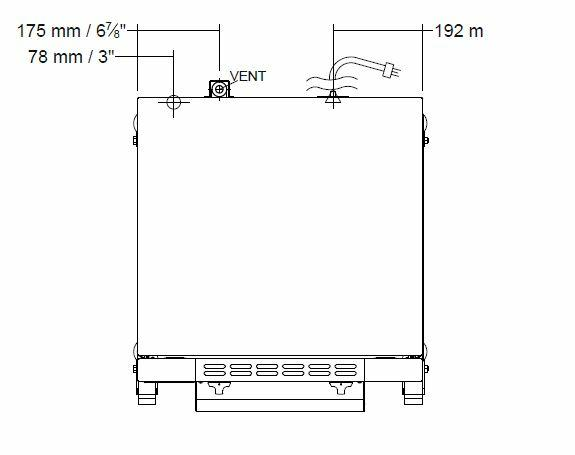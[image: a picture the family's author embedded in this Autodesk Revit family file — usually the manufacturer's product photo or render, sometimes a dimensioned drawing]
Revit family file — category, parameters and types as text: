
# Revit family: QF_MOFFAT_E30M3-SK2731N_UK
name_source: partatom
category: Specialty Equipment
revit_build: Autodesk Revit 2014 (Build: 20130308_1515(x64)
units: mm (PartAtom-declared; Revit-internal decimal feet)

## types (1)
- QF_MOFFAT_E30M3-SK2731N_UK
    Apparent Power = 2280 VA
    Conn Conduit = Yes
    Depth = 665 mm  [stored 2.18176 ft]
    Description = GN 1/1 MANUAL / ELECTRIC CONVECTION OVEN ON A STAINLESS STEEL STAND
    Elec Conn Connection Height = 0 mm  [stored 0 ft]
    Elec Conn RI Height = 0 mm  [stored 0 ft]
    Electrical Remarks = 230-240V, 50Hz, 1P+N+E, 2.3kW, 9.5A
    Exhaust RI Height = 0 mm  [stored 0 ft]
    Exhaust Static Press = 0.00 in-wg
    Exhaust Vent Depth = 0 mm  [stored 0 ft]
    Exhaust Vent Diameter = 0 mm  [stored 0 ft]
    Exhaust Vent Width = 0 mm  [stored 0 ft]
    Exhaust Volume = 0 CFM
    FL Amps = 10 A
    Foodservice Equipment Identifier = Yes
    Height = 1508 mm  [stored 4.94751 ft]
    Height of Stand = 880 mm  [stored 2.88714 ft]
    Identify Quantity as Lot = Yes
    Length = 810 mm
    Manufacturer = MOFFAT
    Max Overcurrent Protection = 0 A
    Min Ckt Ampacity = 0 A
    Model = E30M3-SK2731N
    Number of Poles = 1
    Phase = 1
    Volts = 240 V
    Watts = 2300 W
    Weight in Pounds = 0

note: [stored X ft] marks values corroborated as IEEE doubles in the binary element streams (Revit-internal decimal feet)

## geometry (parser evidence)
native form markers: Blend x12, Sweep x13
no freeform markers — native parametric forms only
